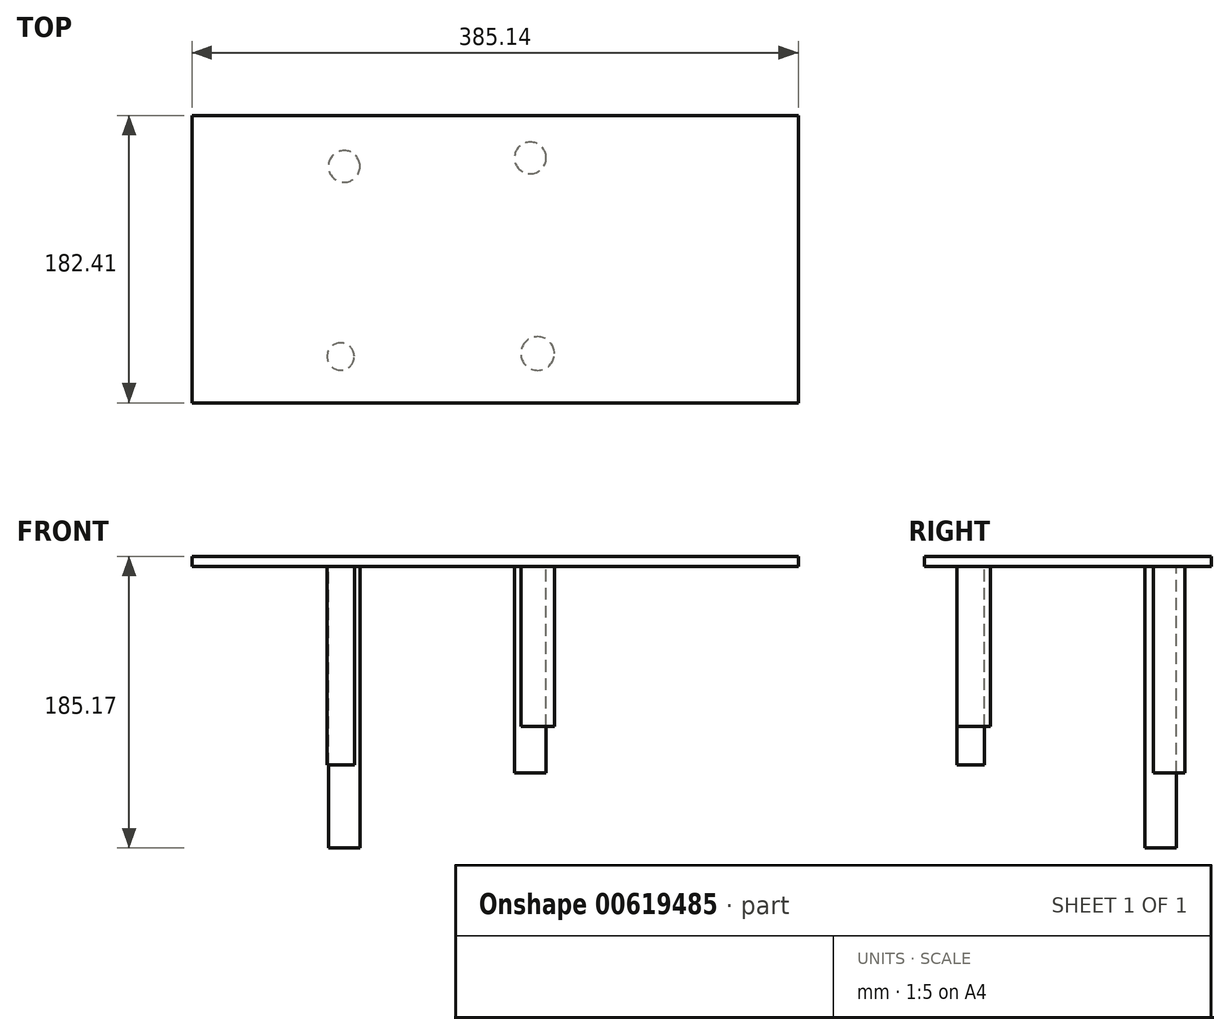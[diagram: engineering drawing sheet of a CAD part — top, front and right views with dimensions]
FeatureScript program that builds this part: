
annotation { "Feature Type Name" : "Feature", "Feature Type Description" : "" }
export const myFeature = defineFeature(function(context is Context, id is Id, definition is map)
    precondition{}
    {
        {
            var Q0;
            Q0=qCreatedBy(makeId("Top.planeOp"),FACE);
            var sketch = newSketch(context, id + "F0", { "sketchPlane" : qUnion([Q0])});
            skCircle(sketch, "E0", {"center": v(-65.04, 58.72) * mm, "radius": 10.05 * mm});
            skSolve(sketch);
        }
        {
            var Q0;
            Q0 = qSketchRegion(id + "F0", true);
            extrude(context, id + "F1", {"entities" : qUnion([Q0]), "oppositeDirection" : true, "depth" : 178.82 * mm, "offsetDistance" : 25.4 * mm});
        }
        {
            var Q0;
            Q0=qCreatedBy(makeId("Top.planeOp"),FACE);
            var sketch = newSketch(context, id + "F2", { "sketchPlane" : qUnion([Q0])});
            skCircle(sketch, "E1", {"center": v(53.19, 64.12) * mm, "radius": 10.05 * mm});
            skSolve(sketch);
        }
        {
            var Q0;
            Q0 = qSketchRegion(id + "F2", true);
            extrude(context, id + "F3", {"entities" : qUnion([Q0]), "oppositeDirection" : true, "depth" : 131.06 * mm, "offsetDistance" : 25.4 * mm});
        }
        {
            var Q0;
            Q0=qCreatedBy(makeId("Top.planeOp"),FACE);
            var sketch = newSketch(context, id + "F4", { "sketchPlane" : qUnion([Q0])});
            skCircle(sketch, "E2", {"center": v(-67.23, -62.05) * mm, "radius": 8.63 * mm});
            skSolve(sketch);
        }
        {
            var Q0;
            Q0 = qSketchRegion(id + "F4", true);
            extrude(context, id + "F5", {"entities" : qUnion([Q0]), "oppositeDirection" : true, "depth" : 125.98 * mm, "offsetDistance" : 25.4 * mm});
        }
        {
            var Q0;
            Q0=qCreatedBy(makeId("Top.planeOp"),FACE);
            var sketch = newSketch(context, id + "F6", { "sketchPlane" : qUnion([Q0])});
            skCircle(sketch, "E3", {"center": v(57.84, -60.16) * mm, "radius": 10.68 * mm});
            skSolve(sketch);
        }
        {
            var Q0;
            Q0 = qSketchRegion(id + "F6", true);
            extrude(context, id + "F7", {"entities" : qUnion([Q0]), "oppositeDirection" : true, "depth" : 101.6 * mm, "offsetDistance" : 25.4 * mm});
        }
        {
            var Q0;
            Q0=qCreatedBy(makeId("Top.planeOp"),FACE);
            var sketch = newSketch(context, id + "F8", { "sketchPlane" : qUnion([Q0])});
            skLineSegment(sketch, "E4.bottom", {"start": v(-161.74, 90.95) * mm, "end": v(223.4, 90.95) * mm});
            skLineSegment(sketch, "E4.top", {"start": v(-161.74, -91.46) * mm, "end": v(223.4, -91.46) * mm});
            skLineSegment(sketch, "E4.left", {"start": v(-161.74, 90.95) * mm, "end": v(-161.74, -91.46) * mm});
            skLineSegment(sketch, "E4.right", {"start": v(223.4, 90.95) * mm, "end": v(223.4, -91.46) * mm});
            skSolve(sketch);
        }
        {
            var Q0;
            Q0 = qSketchRegion(id + "F8", true);
            extrude(context, id + "F9", {"entities" : qUnion([Q0]), "depth" : 6.35 * mm, "offsetDistance" : 25.4 * mm});
        }
    });
